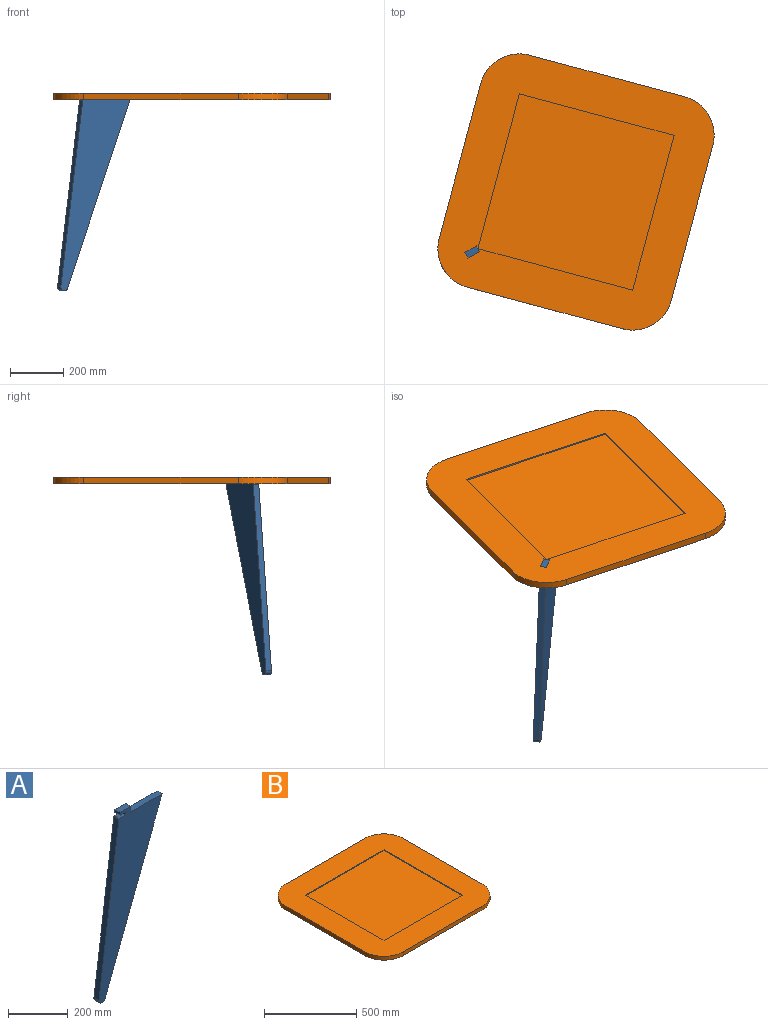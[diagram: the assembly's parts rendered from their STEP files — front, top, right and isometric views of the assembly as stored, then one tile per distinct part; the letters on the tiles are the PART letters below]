
ASSEMBLY  parts=2 mates=1
PART A: 14 faces, bbox 300.1x24x740 mm
  f0: plane 24x23mm, normal (0,0,-1), area 552mm2, adj f1,f11,f12,f13
  f1: plane 24x12mm, normal (-1,0,0), area 288mm2, adj f0,f2,f12,f13
  f2: plane 28.25x24mm, normal (0,0,1), area 678.1mm2, adj f1,f3,f12,f13
  f3: cylinder r=2mm len=24mm, axis (0,-1,0), area 68.9mm2, adj f2,f4,f12,f13
  f4: plane 697.25x94.76mm, normal (-0.99,0,0.13), area 16887.8mm2, adj f3,f5,f12,f13
  f5: cylinder r=15mm len=29mm, axis (0,-1,0), area 1047.7mm2, adj f4,f6,f12,f13
  f6: plane 706.38x271.13mm, normal (0.93,0,-0.36), area 18159mm2, adj f5,f7,f12,f13
  f7: plane 150x24mm, normal (0,0,1), area 3600mm2, adj f6,f8,f12,f13
  f8: plane 24x24mm, normal (1,0,0), area 576mm2, adj f7,f9,f12,f13
  f9: plane 50x24mm, normal (0,0,1), area 1200mm2, adj f8,f10,f12,f13
  f10: plane 24x10mm, normal (-1,0,0), area 240mm2, adj f9,f11,f12,f13
  f11: cylinder r=2mm len=24mm, axis (0,-1,0), area 75.4mm2, adj f0,f10,f12,f13
  f12: plane 740x300.14mm, normal (0,1,0), area 84043.6mm2, adj f0,f1,f2,f3,f4,f5,f6,f7
  f13: plane 740x300.14mm, normal (0,-1,0), area 84043.6mm2, adj f0,f1,f2,f3,f4,f5,f6,f7
PART B: 15 faces, bbox 900x900x25 mm
  f0: plane 900x900mm, normal (0,0,1), area 430685.8mm2, adj f1,f2,f3,f4,f5,f6,f7,f8
  f1: plane 600x25mm, normal (0,-1,0), area 15000mm2, adj f0,f2,f8,f9
  f2: cylinder r=150mm len=150mm, axis (0,0,1), area 5890.5mm2, adj f0,f1,f3,f9
  f3: plane 600x25mm, normal (1,0,0), area 15000mm2, adj f0,f2,f4,f9
  f4: cylinder r=150mm len=150mm, axis (0,0,1), area 5890.5mm2, adj f0,f3,f5,f9
  f5: plane 600x25mm, normal (0,1,0), area 15000mm2, adj f0,f4,f6,f9
  f6: cylinder r=150mm len=150mm, axis (0,0,1), area 5890.5mm2, adj f0,f5,f7,f9
  f7: plane 600x25mm, normal (-1,0,0), area 15000mm2, adj f0,f6,f8,f9
  f8: cylinder r=150mm len=150mm, axis (0,0,1), area 5890.5mm2, adj f0,f1,f7,f9
  f9: plane 900x900mm, normal (0,0,-1), area 790685.8mm2, adj f1,f2,f3,f4,f5,f6,f7,f8
  f10: plane 600x5mm, normal (-1,0,0), area 3000mm2, adj f0,f11,f13,f14
  f11: plane 600x5mm, normal (0,-1,0), area 3000mm2, adj f0,f10,f12,f14
  f12: plane 600x5mm, normal (1,0,0), area 3000mm2, adj f0,f11,f13,f14
  f13: plane 600x5mm, normal (0,1,0), area 3000mm2, adj f0,f10,f12,f14
  f14: plane 600x600mm, normal (0,0,1), area 360000mm2, adj f10,f11,f12,f13
PLACE A rot(axis=(0,0,1),30deg) t=(-100.25,-320.81,-587.54)mm
PLACE B rot(axis=(0,0,-1),15deg) t=(185.14,-142.18,-231.82)mm
MATE revolute A.f9 <-> B.f8  axis (0,0,1) through (-182.28,-354.32,-231.82)mm
